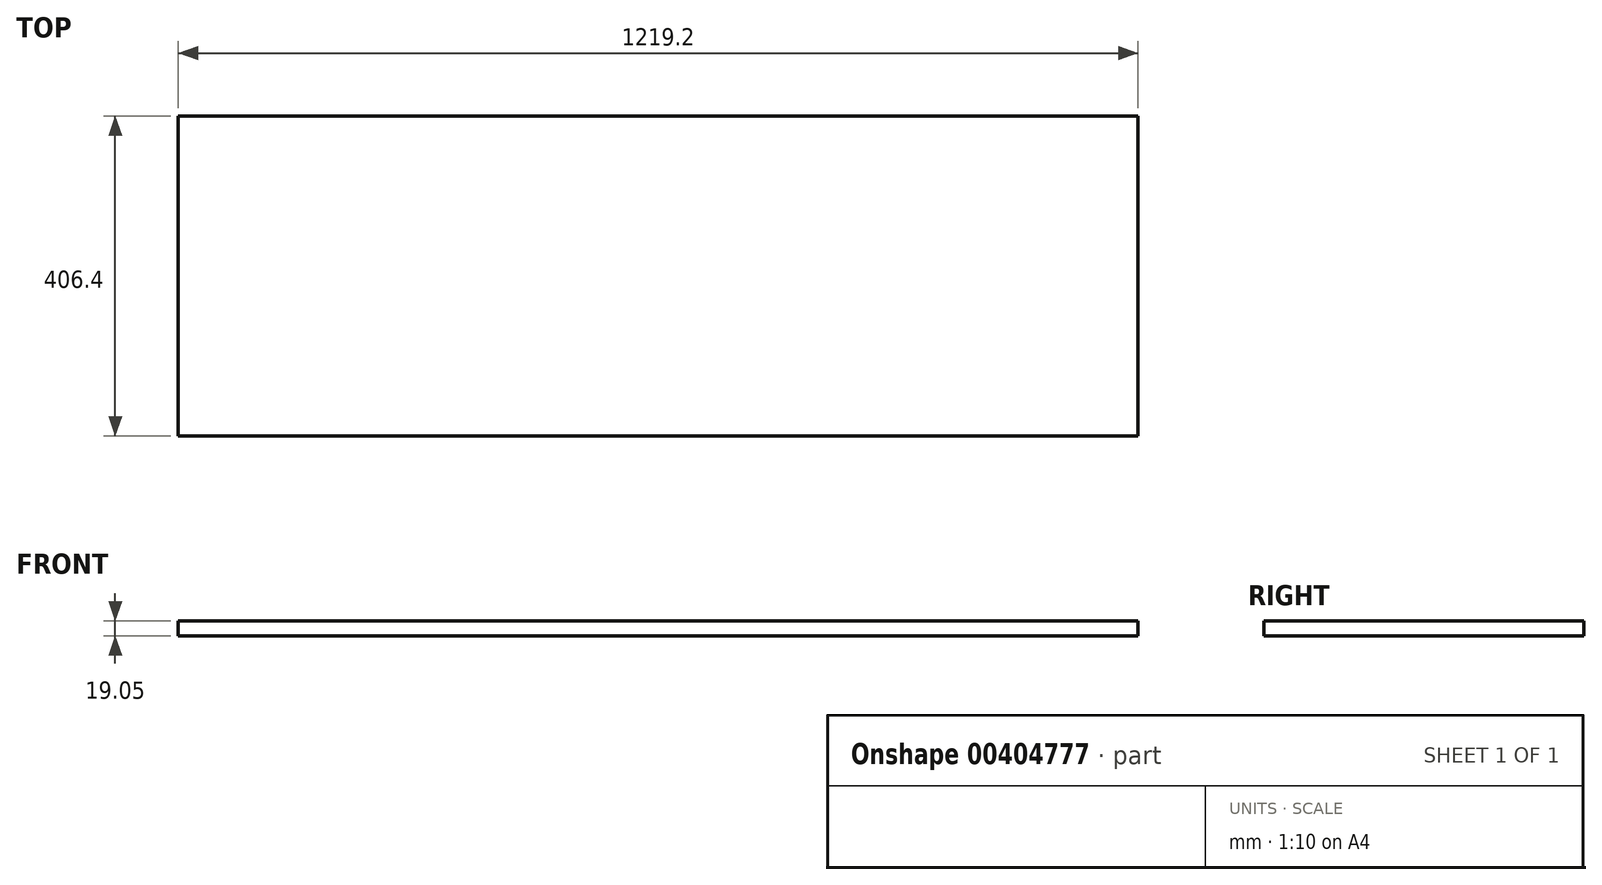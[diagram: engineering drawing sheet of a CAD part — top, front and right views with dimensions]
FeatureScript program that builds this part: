
annotation { "Feature Type Name" : "Feature", "Feature Type Description" : "" }
export const myFeature = defineFeature(function(context is Context, id is Id, definition is map)
    precondition{}
    {
        {
            var Q0;
            Q0=qCreatedBy(makeId("Top.planeOp"),FACE);
            var sketch = newSketch(context, id + "F0", { "sketchPlane" : qUnion([Q0])});
            skLineSegment(sketch, "E0.bottom", {"start": v(609.6, 203.2) * mm, "end": v(-609.6, 203.2) * mm});
            skLineSegment(sketch, "E0.top", {"start": v(609.6, -203.2) * mm, "end": v(-609.6, -203.2) * mm});
            skLineSegment(sketch, "E0.left", {"start": v(609.6, 203.2) * mm, "end": v(609.6, -203.2) * mm});
            skLineSegment(sketch, "E0.right", {"start": v(-609.6, 203.2) * mm, "end": v(-609.6, -203.2) * mm});
            skPoint(sketch, "E0.middle", {"position": v(0, 0) * mm});
            skSolve(sketch);
        }
        {
            var Q0;
            Q0 = qSketchRegion(id + "F0", true);
            extrude(context, id + "F1", {"entities" : qUnion([Q0]), "depth" : 19.05 * mm});
        }
    });
